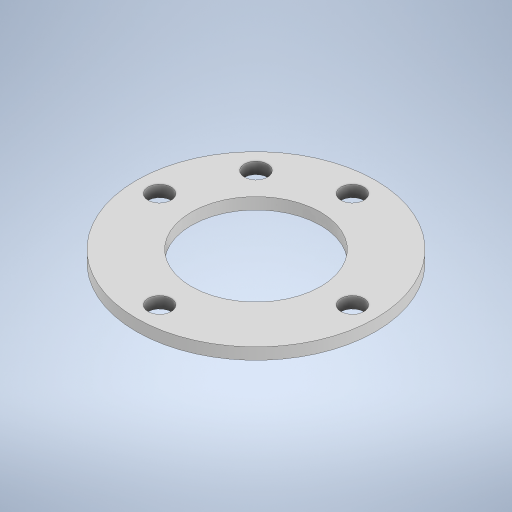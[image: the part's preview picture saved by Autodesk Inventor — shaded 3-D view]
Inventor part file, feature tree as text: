
AUTODESK INVENTOR PART (.ipt)
format: ipt  version: 2023 (Build 270158000, 158)  size: 244,736 bytes
history: native  units: mm
features: extrude x1, sketch x1
ambient origin geometry x8: Origin, YZ Plane, XZ Plane, XY Plane, X Axis, Y Axis, Z Axis, Center Point
bodies: Solid1 (feature_tree)
feature tree (2):
  extrude  "Extrusion1"  Depth=3.0mm
  sketch  "Sketch2"  dims[d0=33.5mm d1=50.0mm d2=62.0mm d3=6.0mm d4=6.0mm d5=45.0deg d6=3.0mm d7=0.0mm]
